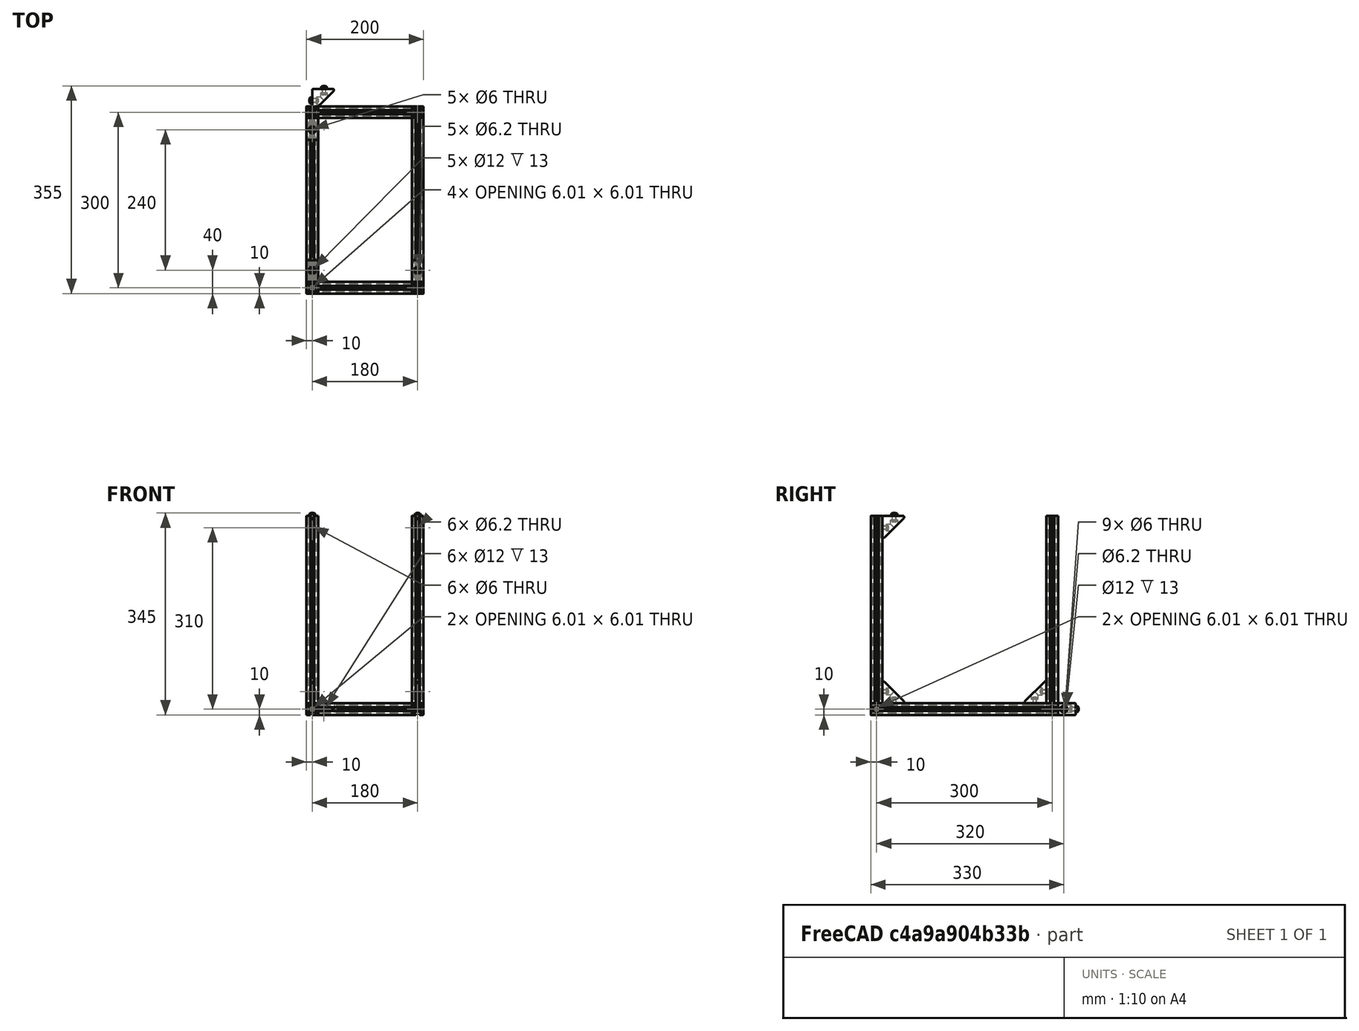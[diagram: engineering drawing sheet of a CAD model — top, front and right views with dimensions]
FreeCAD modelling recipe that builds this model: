
FCSTD DOCUMENT  (FreeCAD 0.17R9796 (Git))
Label: UPKframeNG2b
License: All rights reserved
LicenseURL: http://en.wikipedia.org/wiki/All_rights_reserved
objects: Part::Feature×49, Part::FeaturePython×16, App::Part×6, Part::Compound×5
note: 70 computed .brp shape members not serialized (recipe doc carries the construction recipe); baked Part::Feature solids carry a one-line shape summary decoded from their .brp

FEATURE [Part::Feature] Pocket003001  label="tslot32con"
  Placement = pos=(0,10,10) rot=(1,0,0;1.5708rad)
  shape: bbox 20 x 320 x 20 mm, 150 faces (baked)
FEATURE [Part::Feature] Pocket003002  label="tslot16"
  Placement = pos=(10,0,10) rot=(0,1,0;1.5708rad)
  shape: bbox 160 x 20 x 20 mm, 94 faces (baked)
FEATURE [Part::Feature] Pocket003006  label="tslot16_001"
  Placement = pos=(10,-300,10) rot=(0,1,0;1.5708rad)
  shape: bbox 160 x 20 x 20 mm, 94 faces (baked)
FEATURE [Part::Feature] Pocket003007  label="tslot32con_001"
  Placement = pos=(180,-310,10) rot=(0,0.707107,0.707107;3.14159rad)
  shape: bbox 20 x 320 x 20 mm, 150 faces (baked)
FEATURE [Part::FeaturePython] Screw  label="M6x25-Screw"  # Fasteners workbench fastener (typed FeaturePython)
  Placement = pos=(-4,0,10) rot=(0,-1,0;1.5708rad)
  diameter = 7
  invert = false
  length = 6
  matchOuter = false
  offset = 0
  thread = false
  type = 15
FEATURE [Part::FeaturePython] Screw001  label="M6x25-Screw004"  # Fasteners workbench fastener (typed FeaturePython)
  Placement = pos=(-4,-300,10) rot=(0,-1,0;1.5708rad)
  diameter = 7
  invert = false
  length = 6
  matchOuter = false
  offset = 0
  thread = false
  type = 15
FEATURE [Part::FeaturePython] Screw002  label="M6x25-Screw005"  # Fasteners workbench fastener (typed FeaturePython)
  Placement = pos=(184,0,10) rot=(0,1,0;1.5708rad)
  diameter = 7
  invert = false
  length = 6
  matchOuter = false
  offset = 0
  thread = false
  type = 15
FEATURE [Part::FeaturePython] Screw004  label="M6x25-Screw006"  # Fasteners workbench fastener (typed FeaturePython)
  Placement = pos=(184,-300,10) rot=(0,1,0;1.5708rad)
  diameter = 7
  invert = false
  length = 6
  matchOuter = false
  offset = 0
  thread = false
  type = 15
FEATURE [App::Part] Part  label="lower_frame"
  Group = -> [Pocket003001,Pocket003002,Pocket003006,Pocket003007,Screw,Screw001,Screw002,Screw004]
  License = CC BY 3.0
  LicenseURL = http://creativecommons.org/licenses/by/3.0/
  Origin = -> PartOrigin
FEATURE [Part::Feature] Pocket003008  label="tslot32con001"
  Placement = pos=(0,10,10) rot=(1,0,0;1.5708rad)
  shape: bbox 20 x 320 x 20 mm, 150 faces (baked)
FEATURE [Part::Feature] Pocket003009  label="tslot041"
  Placement = pos=(10,0,10) rot=(0,1,0;1.5708rad)
  shape: bbox 160 x 20 x 20 mm, 94 faces (baked)
FEATURE [Part::Feature] Pocket003010  label="tslot16_002"
  Placement = pos=(10,-300,10) rot=(0,1,0;1.5708rad)
  shape: bbox 160 x 20 x 20 mm, 94 faces (baked)
FEATURE [Part::Feature] Pocket003011  label="tslot32con_002"
  Placement = pos=(180,-310,10) rot=(0,0.707107,0.707107;3.14159rad)
  shape: bbox 20 x 320 x 20 mm, 150 faces (baked)
FEATURE [Part::FeaturePython] Screw005  label="M6x25-Screw007"  # Fasteners workbench fastener (typed FeaturePython)
  Placement = pos=(-4,0,10) rot=(0,-1,0;1.5708rad)
  diameter = 7
  invert = false
  length = 6
  matchOuter = false
  offset = 0
  thread = false
  type = 15
FEATURE [Part::FeaturePython] Screw006  label="M6x25-Screw008"  # Fasteners workbench fastener (typed FeaturePython)
  Placement = pos=(-4,-300,10) rot=(0,-1,0;1.5708rad)
  diameter = 7
  invert = false
  length = 6
  matchOuter = false
  offset = 0
  thread = false
  type = 15
FEATURE [Part::FeaturePython] Screw007  label="M6x25-Screw009"  # Fasteners workbench fastener (typed FeaturePython)
  Placement = pos=(184,0,10) rot=(0,1,0;1.5708rad)
  diameter = 7
  invert = false
  length = 6
  matchOuter = false
  offset = 0
  thread = false
  type = 15
FEATURE [Part::FeaturePython] Screw008  label="M6x25-Screw010"  # Fasteners workbench fastener (typed FeaturePython)
  Placement = pos=(184,-300,10) rot=(0,1,0;1.5708rad)
  diameter = 7
  invert = false
  length = 6
  matchOuter = false
  offset = 0
  thread = false
  type = 15
FEATURE [App::Part] Part001  label="upper_frame"
  Group = -> [Pocket003008,Pocket003009,Pocket003010,Pocket003011,Screw005,Screw006,Screw007,Screw008]
  License = CC BY 3.0
  LicenseURL = http://creativecommons.org/licenses/by/3.0/
  Origin = -> PartOrigin001
  Placement = pos=(0,0,340) rot=(0,0,1;0rad)
FEATURE [Part::Feature] Fillet004001  label="Fillet005"
  shape: bbox 37.5 x 37.5 x 20 mm, 26 faces (baked)
FEATURE [Part::FeaturePython] Screw009  label="M6x12-Screw"  # Fasteners workbench fastener (typed FeaturePython)
  Placement = pos=(7,20,10) rot=(0,1,0;1.5708rad)
  diameter = 4
  invert = false
  length = 1
  matchOuter = false
  offset = 0
  thread = false
  type = 20
FEATURE [Part::Feature] Body001  label="m6nutplate"
  Placement = pos=(-1.5,15,5) rot=(0,-1,0;1.5708rad)
  shape: bbox 3 x 10 x 10 mm, 9 faces (baked)
FEATURE [App::Part] Part002  label="cornerstonescrewnut"
  License = CC BY 3.0
  LicenseURL = http://creativecommons.org/licenses/by/3.0/
  Origin = -> PartOrigin002
  Placement = pos=(10,-50,20) rot=(0,-1,0;1.5708rad)
FEATURE [Part::FeaturePython] Screw010  label="M6x12-Screw001"  # Fasteners workbench fastener (typed FeaturePython)
  Placement = pos=(20,33,10) rot=(1,0,0;1.5708rad)
  diameter = 4
  invert = false
  length = 1
  matchOuter = false
  offset = 0
  thread = false
  type = 20
FEATURE [Part::Feature] Body002  label="m6nutplate001"
  Placement = pos=(15,41.5,5) rot=(0.57735,0.57735,0.57735;4.18879rad)
  shape: bbox 10 x 3 x 10 mm, 9 faces (baked)
FEATURE [Part::Feature] Fillet004002  label="Fillet006"
  shape: bbox 37.5 x 37.5 x 20 mm, 26 faces (baked)
FEATURE [Part::FeaturePython] Screw011  label="M6x12-Screw002"  # Fasteners workbench fastener (typed FeaturePython)
  Placement = pos=(7,20,10) rot=(0,1,0;1.5708rad)
  diameter = 4
  invert = false
  length = 1
  matchOuter = false
  offset = 0
  thread = false
  type = 20
FEATURE [Part::Feature] Body003  label="m6nutplate002"
  Placement = pos=(-1.5,15,5) rot=(0,-1,0;1.5708rad)
  shape: bbox 3 x 10 x 10 mm, 9 faces (baked)
FEATURE [Part::FeaturePython] Screw012  label="M6x12-Screw003"  # Fasteners workbench fastener (typed FeaturePython)
  Placement = pos=(20,33,10) rot=(1,0,0;1.5708rad)
  diameter = 4
  invert = false
  length = 1
  matchOuter = false
  offset = 0
  thread = false
  type = 20
FEATURE [Part::Feature] Body004  label="m6nutplate003"
  Placement = pos=(15,41.5,5) rot=(0.57735,0.57735,0.57735;4.18879rad)
  shape: bbox 10 x 3 x 10 mm, 9 faces (baked)
FEATURE [App::Part] Part003  label="cornerstonescrewnut001"
  Group = -> [Body003,Screw011,Fillet004002,Screw012,Body004,PartOrigin002,Body001,Screw009,Fillet004001,Screw010,Body002,Part002]
  License = CC BY 3.0
  LicenseURL = http://creativecommons.org/licenses/by/3.0/
  Origin = -> PartOrigin003
  Placement = pos=(190,-50,20) rot=(0,-1,0;1.5708rad)
FEATURE [Part::Feature] Fillet004003  label="Fillet007"
  shape: bbox 37.5 x 37.5 x 20 mm, 26 faces (baked)
FEATURE [Part::FeaturePython] Screw013  label="M6x12-Screw004"  # Fasteners workbench fastener (typed FeaturePython)
  Placement = pos=(7,20,10) rot=(0,1,0;1.5708rad)
  diameter = 4
  invert = false
  length = 1
  matchOuter = false
  offset = 0
  thread = false
  type = 20
FEATURE [Part::Feature] Body005  label="m6nutplate004"
  Placement = pos=(-1.5,15,5) rot=(0,-1,0;1.5708rad)
  shape: bbox 3 x 10 x 10 mm, 9 faces (baked)
FEATURE [Part::FeaturePython] Screw014  label="M6x12-Screw005"  # Fasteners workbench fastener (typed FeaturePython)
  Placement = pos=(20,33,10) rot=(1,0,0;1.5708rad)
  diameter = 4
  invert = false
  length = 1
  matchOuter = false
  offset = 0
  thread = false
  type = 20
FEATURE [Part::Feature] Body006  label="m6nutplate005"
  Placement = pos=(15,41.5,5) rot=(0.57735,0.57735,0.57735;4.18879rad)
  shape: bbox 10 x 3 x 10 mm, 9 faces (baked)
FEATURE [App::Part] Part004  label="cornerstonescrewnut002"
  Group = -> [Body005,Screw013,Fillet004003,Screw014,Body006]
  License = CC BY 3.0
  LicenseURL = http://creativecommons.org/licenses/by/3.0/
  Origin = -> PartOrigin004
  Placement = pos=(-10,-50,340) rot=(0,1,0;1.5708rad)
FEATURE [Part::Feature] Fillet004004  label="Fillet008"
  shape: bbox 37.5 x 37.5 x 20 mm, 26 faces (baked)
FEATURE [Part::FeaturePython] Screw015  label="M6x12-Screw006"  # Fasteners workbench fastener (typed FeaturePython)
  Placement = pos=(7,20,10) rot=(0,1,0;1.5708rad)
  diameter = 4
  invert = false
  length = 1
  matchOuter = false
  offset = 0
  thread = false
  type = 20
FEATURE [Part::Feature] Body007  label="m6nutplate006"
  Placement = pos=(-1.5,15,5) rot=(0,-1,0;1.5708rad)
  shape: bbox 3 x 10 x 10 mm, 9 faces (baked)
FEATURE [Part::FeaturePython] Screw016  label="M6x12-Screw007"  # Fasteners workbench fastener (typed FeaturePython)
  Placement = pos=(20,33,10) rot=(1,0,0;1.5708rad)
  diameter = 4
  invert = false
  length = 1
  matchOuter = false
  offset = 0
  thread = false
  type = 20
FEATURE [Part::Feature] Body008  label="m6nutplate007"
  Placement = pos=(15,41.5,5) rot=(0.57735,0.57735,0.57735;4.18879rad)
  shape: bbox 10 x 3 x 10 mm, 9 faces (baked)
FEATURE [App::Part] Part005  label="cornerstonescrewnut003"
  Group = -> [Body007,Screw015,Fillet004004,Screw016,Body008]
  License = CC BY 3.0
  LicenseURL = http://creativecommons.org/licenses/by/3.0/
  Origin = -> PartOrigin005
  Placement = pos=(170,-50,340) rot=(0,1,0;1.5708rad)
FEATURE [Part::Feature] Body009001  label="m6nutplate010"
  Placement = pos=(-1.5,15,5) rot=(0,-1,0;1.5708rad)
  shape: bbox 3 x 10 x 10 mm, 9 faces (baked)
FEATURE [Part::Feature] Body010001  label="m6nutplate011"
  Placement = pos=(15,41.5,5) rot=(0.57735,0.57735,0.57735;4.18879rad)
  shape: bbox 10 x 3 x 10 mm, 9 faces (baked)
FEATURE [Part::Feature] Screw018001  label="M6x12-Screw010"
  Placement = pos=(20,33,10) rot=(1,0,0;1.5708rad)
  shape: bbox 10.5 x 15.3 x 10.5 mm, 15 faces (baked)
FEATURE [Part::Feature] Screw017001  label="M6x12-Screw011"
  Placement = pos=(7,20,10) rot=(0,1,0;1.5708rad)
  shape: bbox 15.3 x 10.5 x 10.5 mm, 15 faces (baked)
FEATURE [Part::Feature] Fillet004005001  label="Fillet010"
  shape: bbox 37.5 x 37.5 x 20 mm, 26 faces (baked)
FEATURE [Part::Compound] Compound
  Links = -> [Body009001,Fillet004005001,Screw017001,Body010001,Screw018001]
  Placement = pos=(10,-250,340) rot=(0.707107,0,-0.707107;3.14159rad)
FEATURE [Part::Feature] Body010002  label="m6nutplate012"
  Placement = pos=(-1.5,15,5) rot=(0,-1,0;1.5708rad)
  shape: bbox 3 x 10 x 10 mm, 9 faces (baked)
FEATURE [Part::Feature] Body010003  label="m6nutplate013"
  Placement = pos=(15,41.5,5) rot=(0.57735,0.57735,0.57735;4.18879rad)
  shape: bbox 10 x 3 x 10 mm, 9 faces (baked)
FEATURE [Part::Feature] Screw018002  label="M6x12-Screw012"
  Placement = pos=(20,33,10) rot=(1,0,0;1.5708rad)
  shape: bbox 10.5 x 15.3 x 10.5 mm, 15 faces (baked)
FEATURE [Part::Feature] Screw018003  label="M6x12-Screw013"
  Placement = pos=(7,20,10) rot=(0,1,0;1.5708rad)
  shape: bbox 15.3 x 10.5 x 10.5 mm, 15 faces (baked)
FEATURE [Part::Feature] Fillet004005002  label="Fillet011"
  shape: bbox 37.5 x 37.5 x 20 mm, 26 faces (baked)
FEATURE [Part::Compound] Compound001
  Links = -> [Body010002,Fillet004005002,Screw018003,Body010003,Screw018002]
  Placement = pos=(190,-250,340) rot=(0.707107,0,-0.707107;3.14159rad)
FEATURE [Part::Feature] Body010004  label="m6nutplate014"
  Placement = pos=(-1.5,15,5) rot=(0,-1,0;1.5708rad)
  shape: bbox 3 x 10 x 10 mm, 9 faces (baked)
FEATURE [Part::Feature] Body010005  label="m6nutplate015"
  Placement = pos=(15,41.5,5) rot=(0.57735,0.57735,0.57735;4.18879rad)
  shape: bbox 10 x 3 x 10 mm, 9 faces (baked)
FEATURE [Part::Feature] Screw018004  label="M6x12-Screw014"
  Placement = pos=(20,33,10) rot=(1,0,0;1.5708rad)
  shape: bbox 10.5 x 15.3 x 10.5 mm, 15 faces (baked)
FEATURE [Part::Feature] Screw018005  label="M6x12-Screw015"
  Placement = pos=(7,20,10) rot=(0,1,0;1.5708rad)
  shape: bbox 15.3 x 10.5 x 10.5 mm, 15 faces (baked)
FEATURE [Part::Feature] Fillet004005003  label="Fillet012"
  shape: bbox 37.5 x 37.5 x 20 mm, 26 faces (baked)
FEATURE [Part::Compound] Compound002
  Links = -> [Body010004,Fillet004005003,Screw018005,Body010005,Screw018004]
  Placement = pos=(10,-290,60) rot=(0.57735,0.57735,-0.57735;4.18879rad)
FEATURE [Part::Feature] Body010006  label="m6nutplate016"
  Placement = pos=(-1.5,15,5) rot=(0,-1,0;1.5708rad)
  shape: bbox 3 x 10 x 10 mm, 9 faces (baked)
FEATURE [Part::Feature] Body010007  label="m6nutplate017"
  Placement = pos=(15,41.5,5) rot=(0.57735,0.57735,0.57735;4.18879rad)
  shape: bbox 10 x 3 x 10 mm, 9 faces (baked)
FEATURE [Part::Feature] Screw018006  label="M6x12-Screw016"
  Placement = pos=(20,33,10) rot=(1,0,0;1.5708rad)
  shape: bbox 10.5 x 15.3 x 10.5 mm, 15 faces (baked)
FEATURE [Part::Feature] Screw018007  label="M6x12-Screw017"
  Placement = pos=(7,20,10) rot=(0,1,0;1.5708rad)
  shape: bbox 15.3 x 10.5 x 10.5 mm, 15 faces (baked)
FEATURE [Part::Feature] Fillet004005004  label="Fillet013"
  shape: bbox 37.5 x 37.5 x 20 mm, 26 faces (baked)
FEATURE [Part::Compound] Compound003
  Links = -> [Body010006,Fillet004005004,Screw018007,Body010007,Screw018006]
  Placement = pos=(190,-290,60) rot=(0.57735,0.57735,-0.57735;4.18879rad)
FEATURE [Part::Feature] Pocket001001  label="tslot32"
  Placement = pos=(0,0,20) rot=(0,0,1;0rad)
  shape: bbox 20 x 20 x 320 mm, 94 faces (baked)
FEATURE [Part::Feature] Body010008  label="m6nutplate018"
  Placement = pos=(-1.5,15,5) rot=(0,-1,0;1.5708rad)
  shape: bbox 3 x 10 x 10 mm, 9 faces (baked)
FEATURE [Part::Feature] Body010009  label="m6nutplate019"
  Placement = pos=(15,41.5,5) rot=(0.57735,0.57735,0.57735;4.18879rad)
  shape: bbox 10 x 3 x 10 mm, 9 faces (baked)
FEATURE [Part::Feature] Screw018008  label="M6x12-Screw018"
  Placement = pos=(20,33,10) rot=(1,0,0;1.5708rad)
  shape: bbox 10.5 x 15.3 x 10.5 mm, 15 faces (baked)
FEATURE [Part::Feature] Screw018009  label="M6x12-Screw019"
  Placement = pos=(7,20,10) rot=(0,1,0;1.5708rad)
  shape: bbox 15.3 x 10.5 x 10.5 mm, 15 faces (baked)
FEATURE [Part::Feature] Fillet004005005  label="Fillet014"
  shape: bbox 37.5 x 37.5 x 20 mm, 26 faces (baked)
FEATURE [Part::Compound] Compound004
  Links = -> [Body010008,Fillet004005005,Screw018009,Body010009,Screw018008]
  Placement = pos=(-10,-10,60) rot=(0.57735,-0.57735,0.57735;4.18879rad)
FEATURE [Part::Feature] Pocket003012  label="tslot32_001"
  Placement = pos=(0,-300,20) rot=(0,0,1;0rad)
  shape: bbox 20 x 20 x 320 mm, 94 faces (baked)
FEATURE [Part::Feature] Pocket003013  label="tslot32_002"
  Placement = pos=(180,0,20) rot=(0,0,1;0rad)
  shape: bbox 20 x 20 x 320 mm, 94 faces (baked)
FEATURE [Part::Feature] Pocket003014  label="tslot32_003"
  Placement = pos=(180,-300,20) rot=(0,0,1;0rad)
  shape: bbox 20 x 20 x 320 mm, 94 faces (baked)
